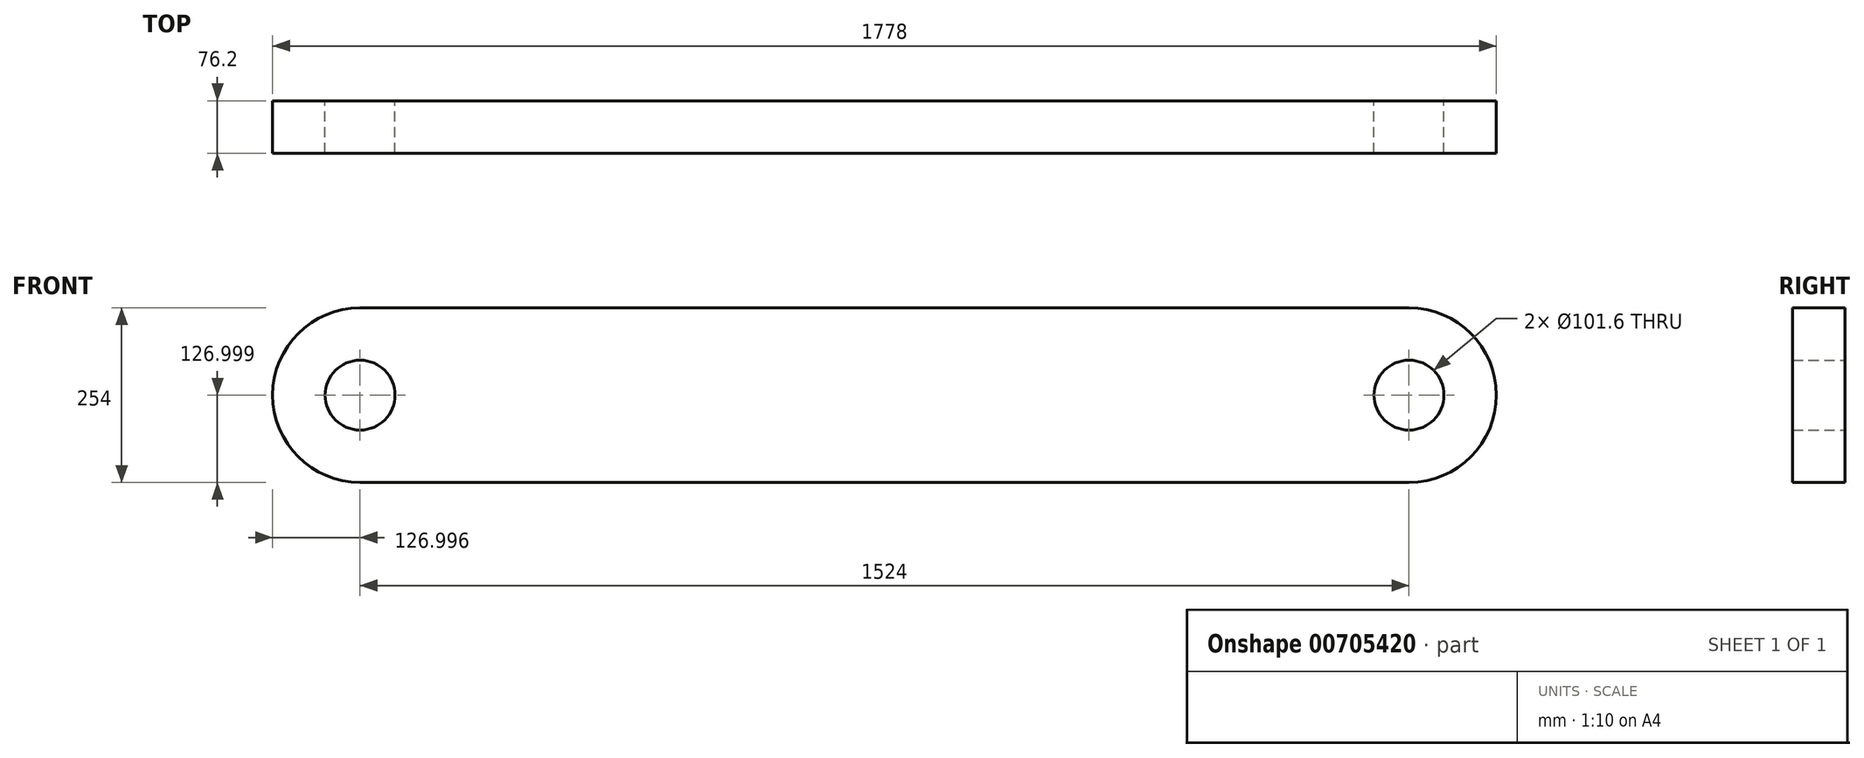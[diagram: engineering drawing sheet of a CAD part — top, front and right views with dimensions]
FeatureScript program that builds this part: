
annotation { "Feature Type Name" : "Feature", "Feature Type Description" : "" }
export const myFeature = defineFeature(function(context is Context, id is Id, definition is map)
    precondition{}
    {
        {
            var Q0;
            Q0=qCreatedBy(makeId("Front.planeOp"),FACE);
            var sketch = newSketch(context, id + "F0", { "sketchPlane" : qUnion([Q0])});
            skLineSegment(sketch, "E0", {"start": v(-758.71, 129.56) * mm, "end": v(765.29, 129.56) * mm});
            skLineSegment(sketch, "E1", {"start": v(-758.71, -124.44) * mm, "end": v(765.29, -124.44) * mm});
            skArc(sketch, "E2", {"start": v(-758.71, 129.56) * mm, "mid": v(-885.71, 2.56) * mm, "end": v(-758.71, -124.44) * mm});
            skArc(sketch, "E3", {"start": v(765.29, 129.56) * mm, "mid": v(892.29, 2.56) * mm, "end": v(765.29, -124.44) * mm});
            skCircle(sketch, "E4", {"center": v(-758.71, 2.56) * mm, "radius": 50.8 * mm});
            skCircle(sketch, "E5", {"center": v(765.29, 2.56) * mm, "radius": 50.8 * mm});
            skSolve(sketch);
        }
        {
            var Q0;
            Q0 = qSketchRegion(id + "F0", true);
            extrude(context, id + "F1", {"entities" : qUnion([Q0]), "depth" : 76.2 * mm, "offsetDistance" : 25.4 * mm});
        }
    });
